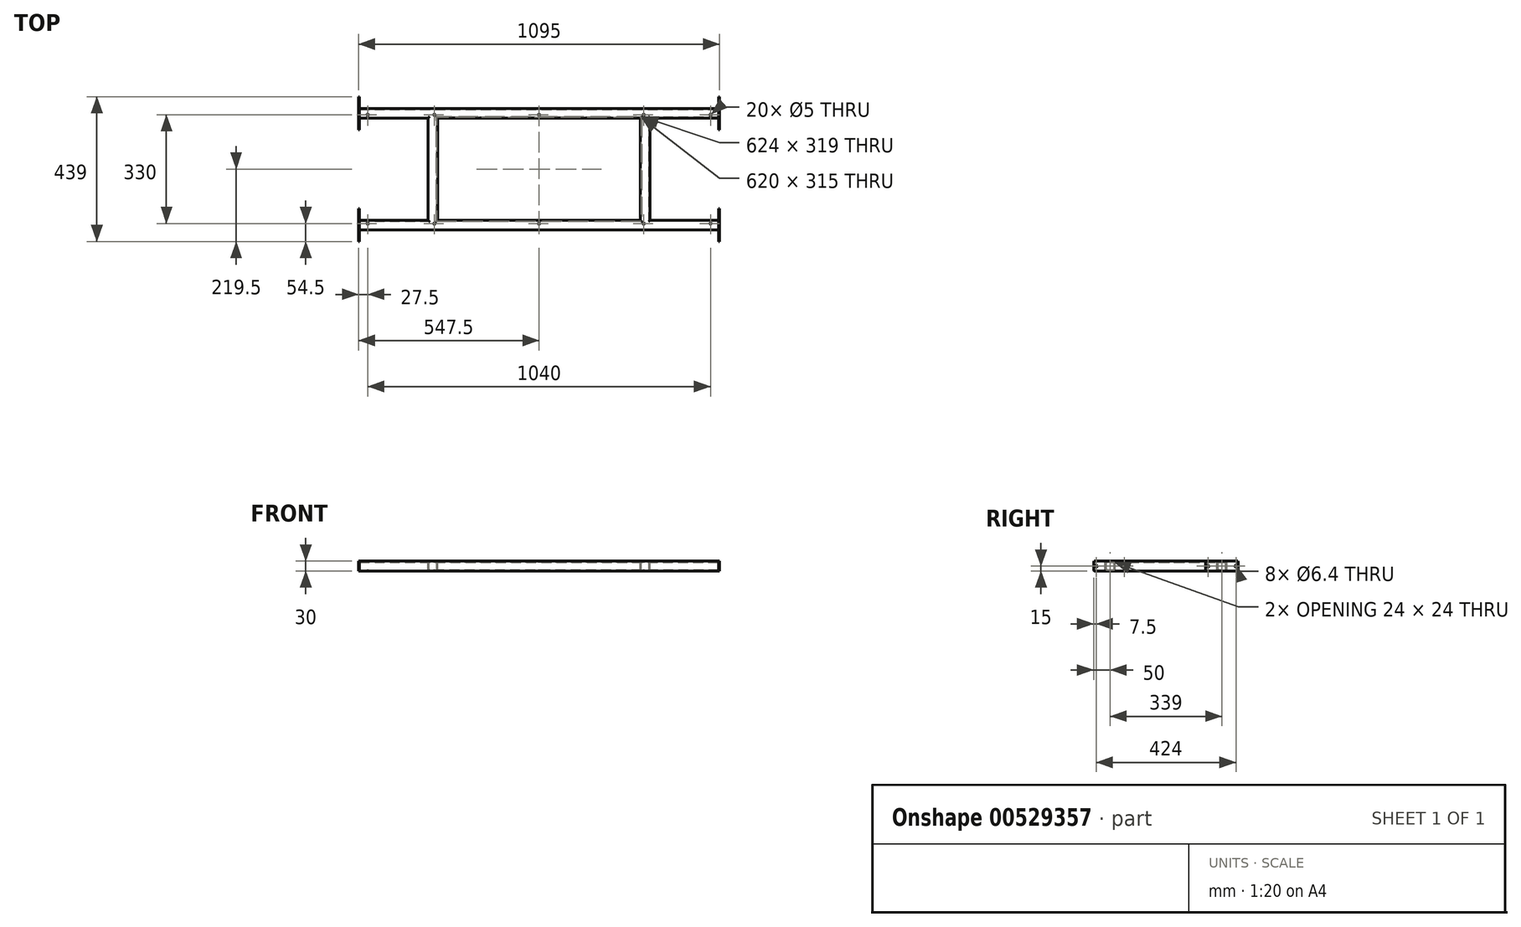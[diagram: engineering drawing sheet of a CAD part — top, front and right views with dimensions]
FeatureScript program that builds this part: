
annotation { "Feature Type Name" : "Feature", "Feature Type Description" : "" }
export const myFeature = defineFeature(function(context is Context, id is Id, definition is map)
    precondition{}
    {
        {
            var Q0;
            Q0=qCreatedBy(makeId("Top.planeOp"),FACE);
            var sketch = newSketch(context, id + "F0", { "sketchPlane" : qUnion([Q0])});
            skPoint(sketch, "E0.middle", {"position": v(0, 0) * mm});
            skLineSegment(sketch, "E1.MirrorCS", {"start": v(-544.5, -154.5) * mm, "end": v(-337, -154.5) * mm});
            skLineSegment(sketch, "E2.bottom", {"start": v(307, -154.5) * mm, "end": v(-307, -154.5) * mm});
            skLineSegment(sketch, "E2.top", {"start": v(307, 154.5) * mm, "end": v(-307, 154.5) * mm});
            skLineSegment(sketch, "E2.left", {"start": v(307, -154.5) * mm, "end": v(307, 154.5) * mm});
            skLineSegment(sketch, "E2.right", {"start": v(-307, -154.5) * mm, "end": v(-307, 154.5) * mm});
            skLineSegment(sketch, "E3", {"start": v(-337, -154.5) * mm, "end": v(-337, 154.5) * mm});
            skLineSegment(sketch, "E4", {"start": v(-544.5, -154.5) * mm, "end": v(-544.5, -184.5) * mm});
            skLineSegment(sketch, "E5", {"start": v(-544.5, -184.5) * mm, "end": v(544.5, -184.5) * mm});
            skLineSegment(sketch, "E6.MirrorCS", {"start": v(-544.5, 154.5) * mm, "end": v(-544.5, 184.5) * mm});
            skLineSegment(sketch, "E7.MirrorCS", {"start": v(-544.5, 154.5) * mm, "end": v(-337, 154.5) * mm});
            skLineSegment(sketch, "E8.MirrorCS", {"start": v(-544.5, 184.5) * mm, "end": v(544.5, 184.5) * mm});
            skLineSegment(sketch, "E9.MirrorCS", {"start": v(544.5, -154.5) * mm, "end": v(544.5, -184.5) * mm});
            skLineSegment(sketch, "E10.MirrorCS", {"start": v(544.5, -154.5) * mm, "end": v(337, -154.5) * mm});
            skLineSegment(sketch, "E11.MirrorCS", {"start": v(544.5, 154.5) * mm, "end": v(544.5, 184.5) * mm});
            skLineSegment(sketch, "E12.MirrorCS", {"start": v(337, -154.5) * mm, "end": v(337, 154.5) * mm});
            skLineSegment(sketch, "E13.MirrorCS", {"start": v(544.5, 154.5) * mm, "end": v(337, 154.5) * mm});
            skSolve(sketch);
        }
        {
            var Q0;
            Q0=makeQuery(id+"F0.imprint","IMPRINT",FACE,{"disambiguationData":[TD([[makeQuery(id+"F0.imprint","IMPRINT",EDGE,{"derivedFrom":sQuery(id+"F0.wireOp",EDGE,"E1.MirrorCS")}),-1.0]])]});
            extrude(context, id + "F1", {"entities" : qUnion([Q0]), "oppositeDirection" : true, "depth" : 30 * mm, "offsetDistance" : 25 * mm});
        }
        {
            var Q0;
            Q0=makeQuery(id+"F1.opExtrude","SWEPT_FACE",FACE,{"disambiguationData":[OSD([sQuery(id+"F0.wireOp",EDGE,"E4")])]});
            var Q1;
            Q1=makeQuery(id+"F1.opExtrude","SWEPT_FACE",FACE,{"disambiguationData":[OSD([sQuery(id+"F0.wireOp",EDGE,"E6.MirrorCS")])]});
            var Q2;
            Q2=makeQuery(id+"F1.opExtrude","SWEPT_FACE",FACE,{"disambiguationData":[OSD([sQuery(id+"F0.wireOp",EDGE,"E11.MirrorCS")])]});
            var Q3;
            Q3=makeQuery(id+"F1.opExtrude","SWEPT_FACE",FACE,{"disambiguationData":[OSD([sQuery(id+"F0.wireOp",EDGE,"E9.MirrorCS")])]});
            shell(context, id + "F2", {"entities" : qUnion([Q0, Q1, Q2, Q3]), "thickness" : 3 * mm});
        }
        {
            var Q0;
            Q0=makeQuery(id+"F1.opExtrude","SWEPT_FACE",FACE,{"disambiguationData":[OSD([sQuery(id+"F0.wireOp",EDGE,"E4")])]});
            var sketch = newSketch(context, id + "F3", { "sketchPlane" : qUnion([Q0])});
            skLineSegment(sketch, "E14.bottom", {"start": v(219.5, -30) * mm, "end": v(119.5, -30) * mm});
            skLineSegment(sketch, "E14.top", {"start": v(219.5, 0) * mm, "end": v(119.5, 0) * mm});
            skLineSegment(sketch, "E14.left", {"start": v(219.5, -30) * mm, "end": v(219.5, 0) * mm});
            skLineSegment(sketch, "E14.right", {"start": v(119.5, -30) * mm, "end": v(119.5, 0) * mm});
            skPoint(sketch, "E14.middle", {"position": v(169.5, -15) * mm});
            skPoint(sketch, "E14.middle.positionSnap0", {"position": v(181.5, -15) * mm});
            skPoint(sketch, "E14.middle.positionSnap1", {"position": v(169.5, -27) * mm});
            skPoint(sketch, "E14.centerSnap0", {"position": v(181.5, -15) * mm});
            skPoint(sketch, "E14.centerSnap1", {"position": v(169.5, -27) * mm});
            skSolve(sketch);
        }
        {
            var Q0;
            {var subQ2=sQuery(id+"F3.wireOp",EDGE,"E14.left");Q0=makeQuery(id+"F3.imprint","IMPRINT",FACE,{"disambiguationData":[TD([[makeQuery(id+"F3.imprint","IMPRINT",EDGE,{"derivedFrom":subQ2}),1.0]])]});}
            var Q1;
            {var subQ0=sQuery(id+"F0.wireOp",EDGE,"E4");Q1=makeQuery(id+"F3.imprint","IMPRINT",FACE,{"disambiguationData":[TD([[makeQuery(id+"F3.imprint","IMPRINT",EDGE,{"derivedFrom":makeQuery(id+"F2.opShell","OFFSET_EDGE",EDGE,{"disambiguationData":[OSD([subQ0]),TDD([makeQuery(id+"F1.opExtrude","CAP_EDGE",EDGE,{"disambiguationData":[OSD([subQ0])],"isStart":true})])]})}),-1.0]])]});}
            var Q2;
            {var subQ2=sQuery(id+"F3.wireOp",EDGE,"E14.right");Q2=makeQuery(id+"F3.imprint","IMPRINT",FACE,{"disambiguationData":[TD([[makeQuery(id+"F3.imprint","IMPRINT",EDGE,{"derivedFrom":subQ2}),-1.0]])]});}
            var Q3;
            {var subQ0=sQuery(id+"F0.wireOp",EDGE,"E4");Q3=makeQuery(id+"F3.imprint","IMPRINT",FACE,{"disambiguationData":[TD([[makeQuery(id+"F3.imprint","IMPRINT",EDGE,{"derivedFrom":makeQuery(id+"F2.opShell","OFFSET_EDGE",EDGE,{"disambiguationData":[OSD([subQ0]),TDD([makeQuery(id+"F1.opExtrude","CAP_EDGE",EDGE,{"disambiguationData":[OSD([subQ0])],"isStart":true})])]})}),1.0]])]});}
            extrude(context, id + "F4", {"entities" : qUnion([Q0, Q1, Q2, Q3]), "depth" : 3 * mm, "offsetDistance" : 25 * mm});
        }
        {
            var Q0;
            Q0=makeQuery(id+"F4.opExtrude","CAP_FACE",FACE,{"disambiguationData":[OSD([sQuery(id+"F3.wireOp",EDGE,"E14.bottom"),sQuery(id+"F3.wireOp",EDGE,"E14.top"),sQuery(id+"F3.wireOp",EDGE,"E14.left"),sQuery(id+"F3.wireOp",EDGE,"E14.right")])],"isStart":false});
            var sketch = newSketch(context, id + "F5", { "sketchPlane" : qUnion([Q0])});
            skLineSegment(sketch, "E15.bottom", {"start": v(212, -22.5) * mm, "end": v(127, -22.5) * mm, "construction": true});
            skLineSegment(sketch, "E15.top", {"start": v(212, -7.5) * mm, "end": v(127, -7.5) * mm, "construction": true});
            skLineSegment(sketch, "E15.left", {"start": v(212, -22.5) * mm, "end": v(212, -7.5) * mm, "construction": true});
            skLineSegment(sketch, "E15.right", {"start": v(127, -22.5) * mm, "end": v(127, -7.5) * mm, "construction": true});
            skPoint(sketch, "E15.middle", {"position": v(169.5, -15) * mm});
            skPoint(sketch, "E15.middle.positionSnap0", {"position": v(169.5, -30) * mm});
            skPoint(sketch, "E15.middle.positionSnap1", {"position": v(119.5, -15) * mm});
            skPoint(sketch, "E15.centerSnap0", {"position": v(169.5, -30) * mm});
            skPoint(sketch, "E15.centerSnap1", {"position": v(119.5, -15) * mm});
            skPoint(sketch, "E16", {"position": v(127, -15) * mm});
            skPoint(sketch, "E17", {"position": v(212, -15) * mm});
            skSolve(sketch);
        }
        {
            var Q0;
            Q0=makeQuery(id+"F4.opExtrude","SWEPT_EDGE",EDGE,{"disambiguationData":[OSD([sQuery(id+"F3.wireOp",EDGE,"E14.bottom"),sQuery(id+"F3.wireOp",EDGE,"E14.left")])]});
            var Q1;
            Q1=makeQuery(id+"F4.opExtrude","SWEPT_EDGE",EDGE,{"disambiguationData":[OSD([sQuery(id+"F3.wireOp",EDGE,"E14.top"),sQuery(id+"F3.wireOp",EDGE,"E14.left")])]});
            var Q2;
            Q2=makeQuery(id+"F4.opExtrude","SWEPT_EDGE",EDGE,{"disambiguationData":[OSD([sQuery(id+"F3.wireOp",EDGE,"E14.bottom"),sQuery(id+"F3.wireOp",EDGE,"E14.right")])]});
            var Q3;
            Q3=makeQuery(id+"F4.opExtrude","SWEPT_EDGE",EDGE,{"disambiguationData":[OSD([sQuery(id+"F3.wireOp",EDGE,"E14.top"),sQuery(id+"F3.wireOp",EDGE,"E14.right")])]});
            chamfer(context, id + "F6", {"entities" : qUnion([Q0, Q1, Q2, Q3]), "width" : 2 * mm, "tangentPropagation" : true});
        }
        {
            var Q0;
            Q0=makeQuery(id+"F1.opExtrude","CAP_EDGE",EDGE,{"disambiguationData":[OSD([sQuery(id+"F0.wireOp",EDGE,"E5")])],"isStart":false});
            var Q1;
            Q1=makeQuery(id+"F1.opExtrude","CAP_EDGE",EDGE,{"disambiguationData":[OSD([sQuery(id+"F0.wireOp",EDGE,"E1.MirrorCS")])],"isStart":false});
            var Q2;
            Q2=makeQuery(id+"F1.opExtrude","CAP_EDGE",EDGE,{"disambiguationData":[OSD([sQuery(id+"F0.wireOp",EDGE,"E3")])],"isStart":false});
            var Q3;
            Q3=makeQuery(id+"F1.opExtrude","CAP_EDGE",EDGE,{"disambiguationData":[OSD([sQuery(id+"F0.wireOp",EDGE,"E2.right")])],"isStart":false});
            var Q4;
            Q4=makeQuery(id+"F1.opExtrude","CAP_EDGE",EDGE,{"disambiguationData":[OSD([sQuery(id+"F0.wireOp",EDGE,"E2.bottom")])],"isStart":false});
            var Q5;
            Q5=makeQuery(id+"F1.opExtrude","CAP_EDGE",EDGE,{"disambiguationData":[OSD([sQuery(id+"F0.wireOp",EDGE,"E7.MirrorCS")])],"isStart":false});
            var Q6;
            Q6=makeQuery(id+"F1.opExtrude","CAP_EDGE",EDGE,{"disambiguationData":[OSD([sQuery(id+"F0.wireOp",EDGE,"E8.MirrorCS")])],"isStart":false});
            var Q7;
            Q7=makeQuery(id+"F1.opExtrude","CAP_EDGE",EDGE,{"disambiguationData":[OSD([sQuery(id+"F0.wireOp",EDGE,"E2.left")])],"isStart":false});
            var Q8;
            Q8=makeQuery(id+"F1.opExtrude","CAP_EDGE",EDGE,{"disambiguationData":[OSD([sQuery(id+"F0.wireOp",EDGE,"E12.MirrorCS")])],"isStart":false});
            var Q9;
            Q9=makeQuery(id+"F1.opExtrude","CAP_EDGE",EDGE,{"disambiguationData":[OSD([sQuery(id+"F0.wireOp",EDGE,"E2.top")])],"isStart":false});
            var Q10;
            Q10=makeQuery(id+"F1.opExtrude","CAP_EDGE",EDGE,{"disambiguationData":[OSD([sQuery(id+"F0.wireOp",EDGE,"E13.MirrorCS")])],"isStart":false});
            var Q11;
            Q11=makeQuery(id+"F1.opExtrude","CAP_EDGE",EDGE,{"disambiguationData":[OSD([sQuery(id+"F0.wireOp",EDGE,"E8.MirrorCS")])],"isStart":true});
            var Q12;
            Q12=makeQuery(id+"F1.opExtrude","CAP_EDGE",EDGE,{"disambiguationData":[OSD([sQuery(id+"F0.wireOp",EDGE,"E7.MirrorCS")])],"isStart":true});
            var Q13;
            Q13=makeQuery(id+"F1.opExtrude","CAP_EDGE",EDGE,{"disambiguationData":[OSD([sQuery(id+"F0.wireOp",EDGE,"E2.top")])],"isStart":true});
            var Q14;
            Q14=makeQuery(id+"F1.opExtrude","CAP_EDGE",EDGE,{"disambiguationData":[OSD([sQuery(id+"F0.wireOp",EDGE,"E3")])],"isStart":true});
            var Q15;
            Q15=makeQuery(id+"F1.opExtrude","CAP_EDGE",EDGE,{"disambiguationData":[OSD([sQuery(id+"F0.wireOp",EDGE,"E2.right")])],"isStart":true});
            var Q16;
            Q16=makeQuery(id+"F1.opExtrude","CAP_EDGE",EDGE,{"disambiguationData":[OSD([sQuery(id+"F0.wireOp",EDGE,"E1.MirrorCS")])],"isStart":true});
            var Q17;
            Q17=makeQuery(id+"F1.opExtrude","CAP_EDGE",EDGE,{"disambiguationData":[OSD([sQuery(id+"F0.wireOp",EDGE,"E2.bottom")])],"isStart":true});
            var Q18;
            Q18=makeQuery(id+"F1.opExtrude","CAP_EDGE",EDGE,{"disambiguationData":[OSD([sQuery(id+"F0.wireOp",EDGE,"E2.left")])],"isStart":true});
            var Q19;
            Q19=makeQuery(id+"F1.opExtrude","CAP_EDGE",EDGE,{"disambiguationData":[OSD([sQuery(id+"F0.wireOp",EDGE,"E12.MirrorCS")])],"isStart":true});
            var Q20;
            Q20=makeQuery(id+"F1.opExtrude","CAP_EDGE",EDGE,{"disambiguationData":[OSD([sQuery(id+"F0.wireOp",EDGE,"E10.MirrorCS")])],"isStart":true});
            var Q21;
            Q21=makeQuery(id+"F1.opExtrude","CAP_EDGE",EDGE,{"disambiguationData":[OSD([sQuery(id+"F0.wireOp",EDGE,"E13.MirrorCS")])],"isStart":true});
            var Q22;
            Q22=makeQuery(id+"F1.opExtrude","CAP_EDGE",EDGE,{"disambiguationData":[OSD([sQuery(id+"F0.wireOp",EDGE,"E10.MirrorCS")])],"isStart":false});
            var Q23;
            Q23=makeQuery(id+"F1.opExtrude","CAP_EDGE",EDGE,{"disambiguationData":[OSD([sQuery(id+"F0.wireOp",EDGE,"E5")])],"isStart":true});
            fillet(context, id + "F7", {"entities" : qUnion([Q0, Q1, Q2, Q3, Q4, Q5, Q6, Q7, Q8, Q9, Q10, Q11, Q12, Q13, Q14, Q15, Q16, Q17, Q18, Q19, Q20, Q21, Q22, Q23]), "radius" : 5 * mm, "tangentPropagation" : true, "allowEdgeOverflow" : false});
        }
        {
            var Q0;
            {var subQ0=sQuery(id+"F0.wireOp",EDGE,"E7.MirrorCS");Q0=makeQuery(id+"F2.opShell","OFFSET_EDGE",EDGE,{"disambiguationData":[OSD([subQ0]),TDD([makeQuery(id+"F1.opExtrude","CAP_EDGE",EDGE,{"disambiguationData":[OSD([subQ0])],"isStart":true})])]});}
            var Q1;
            {var subQ0=sQuery(id+"F0.wireOp",EDGE,"E7.MirrorCS");Q1=makeQuery(id+"F2.opShell","OFFSET_EDGE",EDGE,{"disambiguationData":[OSD([subQ0]),TDD([makeQuery(id+"F1.opExtrude","CAP_EDGE",EDGE,{"disambiguationData":[OSD([subQ0])],"isStart":false})])]});}
            var Q2;
            {var subQ0=sQuery(id+"F0.wireOp",EDGE,"E8.MirrorCS");Q2=makeQuery(id+"F2.opShell","OFFSET_EDGE",EDGE,{"disambiguationData":[OSD([subQ0]),TDD([makeQuery(id+"F1.opExtrude","CAP_EDGE",EDGE,{"disambiguationData":[OSD([subQ0])],"isStart":false})])]});}
            var Q3;
            {var subQ0=sQuery(id+"F0.wireOp",EDGE,"E8.MirrorCS");Q3=makeQuery(id+"F2.opShell","OFFSET_EDGE",EDGE,{"disambiguationData":[OSD([subQ0]),TDD([makeQuery(id+"F1.opExtrude","CAP_EDGE",EDGE,{"disambiguationData":[OSD([subQ0])],"isStart":true})])]});}
            var Q4;
            {var subQ0=sQuery(id+"F0.wireOp",EDGE,"E5");Q4=makeQuery(id+"F2.opShell","OFFSET_EDGE",EDGE,{"disambiguationData":[OSD([subQ0]),TDD([makeQuery(id+"F1.opExtrude","CAP_EDGE",EDGE,{"disambiguationData":[OSD([subQ0])],"isStart":true})])]});}
            var Q5;
            {var subQ0=sQuery(id+"F0.wireOp",EDGE,"E10.MirrorCS");Q5=makeQuery(id+"F2.opShell","OFFSET_EDGE",EDGE,{"disambiguationData":[OSD([subQ0]),TDD([makeQuery(id+"F1.opExtrude","CAP_EDGE",EDGE,{"disambiguationData":[OSD([subQ0])],"isStart":true})])]});}
            var Q6;
            {var subQ0=sQuery(id+"F0.wireOp",EDGE,"E10.MirrorCS");Q6=makeQuery(id+"F2.opShell","OFFSET_EDGE",EDGE,{"disambiguationData":[OSD([subQ0]),TDD([makeQuery(id+"F1.opExtrude","CAP_EDGE",EDGE,{"disambiguationData":[OSD([subQ0])],"isStart":false})])]});}
            var Q7;
            {var subQ0=sQuery(id+"F0.wireOp",EDGE,"E5");Q7=makeQuery(id+"F2.opShell","OFFSET_EDGE",EDGE,{"disambiguationData":[OSD([subQ0]),TDD([makeQuery(id+"F1.opExtrude","CAP_EDGE",EDGE,{"disambiguationData":[OSD([subQ0])],"isStart":false})])]});}
            fillet(context, id + "F8", {"entities" : qUnion([Q0, Q1, Q2, Q3, Q4, Q5, Q6, Q7]), "radius" : 3 * mm, "tangentPropagation" : true, "allowEdgeOverflow" : false});
        }
        {
            var Q0;
            {var subQ0=makeQuery(id+"F4.opExtrude","SWEPT_FACE",FACE,{"disambiguationData":[OSD([sQuery(id+"F3.wireOp",EDGE,"E14.top")])]});var subQ1=makeQuery(id+"FVqL0wcbLrHWyjg_2.opPattern","COPY",FACE,{"derivedFrom":subQ0,"instanceName":"1"});Q0=makeQuery(id+"Fumo5sHBrgLQ75w_2.boolean.opBoolean","MERGE",FACE,{"derivedFrom":[subQ0,makeQuery(id+"F1.opExtrude","CAP_FACE",FACE,{"disambiguationData":[OSD([sQuery(id+"F0.wireOp",EDGE,"E1.MirrorCS"),sQuery(id+"F0.wireOp",EDGE,"E2.bottom"),sQuery(id+"F0.wireOp",EDGE,"E2.top"),sQuery(id+"F0.wireOp",EDGE,"E2.left"),sQuery(id+"F0.wireOp",EDGE,"E2.right"),sQuery(id+"F0.wireOp",EDGE,"E3"),sQuery(id+"F0.wireOp",EDGE,"E4"),sQuery(id+"F0.wireOp",EDGE,"E5"),sQuery(id+"F0.wireOp",EDGE,"E6.MirrorCS"),sQuery(id+"F0.wireOp",EDGE,"E7.MirrorCS"),sQuery(id+"F0.wireOp",EDGE,"E8.MirrorCS"),sQuery(id+"F0.wireOp",EDGE,"E9.MirrorCS"),sQuery(id+"F0.wireOp",EDGE,"E10.MirrorCS"),sQuery(id+"F0.wireOp",EDGE,"E11.MirrorCS"),sQuery(id+"F0.wireOp",EDGE,"E12.MirrorCS"),sQuery(id+"F0.wireOp",EDGE,"E13.MirrorCS")])],"isStart":true}),subQ1,makeQuery(id+"Fumo5sHBrgLQ75w_2.opPattern","COPY",FACE,{"derivedFrom":subQ0,"instanceName":"1"}),makeQuery(id+"Fumo5sHBrgLQ75w_2.opPattern","COPY",FACE,{"derivedFrom":subQ1,"instanceName":"1"})]});}
            var sketch = newSketch(context, id + "F9", { "sketchPlane" : qUnion([Q0])});
            skLineSegment(sketch, "E18.bottom", {"start": v(-317.5, 165) * mm, "end": v(317.5, 165) * mm, "construction": true});
            skLineSegment(sketch, "E18.top", {"start": v(-317.5, -165) * mm, "end": v(317.5, -165) * mm, "construction": true});
            skLineSegment(sketch, "E18.left", {"start": v(-317.5, 165) * mm, "end": v(-317.5, -165) * mm, "construction": true});
            skLineSegment(sketch, "E18.right", {"start": v(317.5, 165) * mm, "end": v(317.5, -165) * mm, "construction": true});
            skPoint(sketch, "E18.middle", {"position": v(0, 0) * mm});
            skPoint(sketch, "E19", {"position": v(-317.5, 165) * mm});
            skPoint(sketch, "E20", {"position": v(-317.5, -165) * mm});
            skPoint(sketch, "E21", {"position": v(0, 165) * mm});
            skPoint(sketch, "E22", {"position": v(317.5, 165) * mm});
            skPoint(sketch, "E23", {"position": v(317.5, -165) * mm});
            skPoint(sketch, "E24", {"position": v(0, -165) * mm});
            skPoint(sketch, "E25", {"position": v(-520, 165) * mm});
            skPoint(sketch, "E26", {"position": v(520, 165) * mm});
            skPoint(sketch, "E27", {"position": v(520, -165) * mm});
            skPoint(sketch, "E28", {"position": v(-520, -165) * mm});
            skSolve(sketch);
        }
        {
            var Q0;
            Q0=sQuery(id+"F5.wireOp",VERTEX,"E16");
            var Q1;
            Q1=sQuery(id+"F5.wireOp",VERTEX,"E17");
            var Q2;
            Q2=makeQuery(id+"F4.opExtrude","SWEPT_BODY",BODY,{"disambiguationData":[OSD([sQuery(id+"F3.wireOp",EDGE,"E14.bottom"),sQuery(id+"F3.wireOp",EDGE,"E14.top"),sQuery(id+"F3.wireOp",EDGE,"E14.left"),sQuery(id+"F3.wireOp",EDGE,"E14.right")])]});
            hole(context, id + "F10", {"style" : HoleStyle.SIMPLE, "endStyle" : HoleEndStyle.BLIND, "holeDiameter" : 6.4 * mm, "holeDepth" : 3 * mm, "isTappedThrough" : true, "tappedDepth" : 9 * mm, "tapClearance" : 3, "startFromSketch" : true, "locations" : qUnion([Q0, Q1]), "scope" : qUnion([Q2])});
        }
        {
            var Q0;
            Q0=makeQuery(id+"F4.opExtrude","SWEPT_BODY",BODY,{"disambiguationData":[OSD([sQuery(id+"F3.wireOp",EDGE,"E14.bottom"),sQuery(id+"F3.wireOp",EDGE,"E14.top"),sQuery(id+"F3.wireOp",EDGE,"E14.left"),sQuery(id+"F3.wireOp",EDGE,"E14.right")])]});
            var Q1;
            Q1=qCreatedBy(makeId("Right.planeOp"),FACE);
            mirror(context, id + "F11", {"entities" : qUnion([Q0]), "mirrorPlane" : qUnion([Q1])});
        }
        {
            var Q0;
            Q0=makeQuery(id+"F4.opExtrude","SWEPT_BODY",BODY,{"disambiguationData":[OSD([sQuery(id+"F3.wireOp",EDGE,"E14.bottom"),sQuery(id+"F3.wireOp",EDGE,"E14.top"),sQuery(id+"F3.wireOp",EDGE,"E14.left"),sQuery(id+"F3.wireOp",EDGE,"E14.right")])]});
            var Q1;
            Q1=makeQuery(id+"F11.opPattern","COPY",BODY,{"derivedFrom":makeQuery(id+"F4.opExtrude","SWEPT_BODY",BODY,{"disambiguationData":[OSD([sQuery(id+"F3.wireOp",EDGE,"E14.bottom"),sQuery(id+"F3.wireOp",EDGE,"E14.top"),sQuery(id+"F3.wireOp",EDGE,"E14.left"),sQuery(id+"F3.wireOp",EDGE,"E14.right")])]}),"instanceName":"1"});
            var Q2;
            Q2=qCreatedBy(makeId("Front.planeOp"),FACE);
            mirror(context, id + "F12", {"entities" : qUnion([Q0, Q1]), "mirrorPlane" : qUnion([Q2])});
        }
        {
            var Q0;
            Q0=sQuery(id+"F9.wireOp",VERTEX,"E25");
            var Q1;
            Q1=sQuery(id+"F9.wireOp",VERTEX,"E19");
            var Q2;
            Q2=sQuery(id+"F9.wireOp",VERTEX,"E21");
            var Q3;
            Q3=sQuery(id+"F9.wireOp",VERTEX,"E22");
            var Q4;
            Q4=sQuery(id+"F9.wireOp",VERTEX,"E26");
            var Q5;
            Q5=sQuery(id+"F9.wireOp",VERTEX,"E27");
            var Q6;
            Q6=sQuery(id+"F9.wireOp",VERTEX,"E23");
            var Q7;
            Q7=sQuery(id+"F9.wireOp",VERTEX,"E24");
            var Q8;
            Q8=sQuery(id+"F9.wireOp",VERTEX,"E20");
            var Q9;
            Q9=sQuery(id+"F9.wireOp",VERTEX,"E28");
            var Q10;
            Q10=makeQuery(id+"F1.opExtrude","SWEPT_BODY",BODY,{"disambiguationData":[OSD([sQuery(id+"F0.wireOp",EDGE,"E1.MirrorCS"),sQuery(id+"F0.wireOp",EDGE,"E2.bottom"),sQuery(id+"F0.wireOp",EDGE,"E2.top"),sQuery(id+"F0.wireOp",EDGE,"E2.left"),sQuery(id+"F0.wireOp",EDGE,"E2.right"),sQuery(id+"F0.wireOp",EDGE,"E3"),sQuery(id+"F0.wireOp",EDGE,"E4"),sQuery(id+"F0.wireOp",EDGE,"E5"),sQuery(id+"F0.wireOp",EDGE,"E6.MirrorCS"),sQuery(id+"F0.wireOp",EDGE,"E7.MirrorCS"),sQuery(id+"F0.wireOp",EDGE,"E8.MirrorCS"),sQuery(id+"F0.wireOp",EDGE,"E9.MirrorCS"),sQuery(id+"F0.wireOp",EDGE,"E10.MirrorCS"),sQuery(id+"F0.wireOp",EDGE,"E11.MirrorCS"),sQuery(id+"F0.wireOp",EDGE,"E12.MirrorCS"),sQuery(id+"F0.wireOp",EDGE,"E13.MirrorCS")])]});
            hole(context, id + "F13", {"style" : HoleStyle.SIMPLE, "endStyle" : HoleEndStyle.THROUGH, "standardTappedOrClearance" : lookupTablePath({ "standard" : "ISO", "engagement" : "75%", "pitch" : "1 mm", "size" : "M6", "type" : "Tapped" }), "standardBlindInLast" : lookupTablePath({ "standard" : "ISO", "engagement" : "75%", "pitch" : "1 mm", "size" : "M6", "type" : "Tapped" }), "holeDiameter" : 5 * mm, "showTappedDepth" : true, "isTappedThrough" : true, "tappedDepth" : 9 * mm, "tapClearance" : 3, "startFromSketch" : true, "locations" : qUnion([Q0, Q1, Q2, Q3, Q4, Q5, Q6, Q7, Q8, Q9]), "scope" : qUnion([Q10]), "majorDiameter" : 6 * mm});
        }
    });
